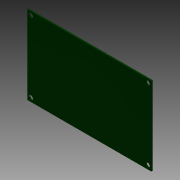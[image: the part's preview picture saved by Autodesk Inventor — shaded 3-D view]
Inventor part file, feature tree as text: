
AUTODESK INVENTOR PART (.ipt)
format: ipt  version: 2013 (Build 170138000, 138)  size: 97,792 bytes
history: native  units: in
note: dims shown in document units (in); Inventor stores cm internally (conversion verified against a paired STEP export)
features: extrude x1, sketch x1
ambient origin geometry x8: Origin, YZ Plane, XZ Plane, XY Plane, X Axis, Y Axis, Z Axis, Center Point
bodies: Solid1 (feature_tree)
feature tree (2):
  extrude  "Extrusion1"  Depth=3.4in
  sketch  "Sketch1"  dims[d0=0.0394in d1=0.0in d2=3.4in d4=2.15in d6=0.1181in d21=0.1in d22=0.1in]
